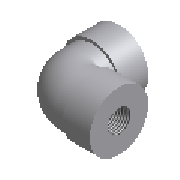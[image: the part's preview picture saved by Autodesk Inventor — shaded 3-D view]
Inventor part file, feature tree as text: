
AUTODESK INVENTOR PART (.ipt)
format: ipt  version: 2023.2 (Build 272271030, 271C)  size: 267,264 bytes
history: native  units: mm (DEFAULTED — no unit token found)
features: other x6, revolve x4, sketch x2
ambient origin geometry x8: Origin, YZ Plane, XZ Plane, XY Plane, X Axis, Y Axis, Z Axis, Center Point
bodies: Solid1 (feature_tree)
feature tree (12):
  sketch  "Sketch1"  dims[d0=18.320766mm d1=38.1mm d2=0.312398mm d3=0.312398mm]
  sketch  "Sketch2"  dims[d4=18.320766mm d5=38.1mm d6=13.55598mm d7=26.1112mm d8=13.55598mm d9=26.1112mm d10=0.0mm d11=9.9822mm d12=9.9822mm d13=17.145mm d14=0.0mm d101=90.0deg d102=90.0deg d105=25.4mm d106=0.0mm d107=25.4mm d108=0.0mm d15=33.274mm d16=16.637mm d17=33.274mm d18=16.637mm d19=34.29mm d20=34.29mm d21=9.9822mm d116=90.0deg d117=90.0deg d22=13.055641mm d23=0.0mm d122=0.0mm d123=0.0mm]
  revolve  "Revolve1"  [1 undecoded]
  revolve  "Revolve2"  [1 undecoded]
  revolve  "Revolve3"  [1 undecoded]
  revolve  "Revolve4"  [1 undecoded]
  other  "Work Axis1"
  other  "Work Point1"
  other  "Work Point2"
  other  "Work Axis2"
  other  "Work Point3"
  other  "Work Point4"
note: 4 required parameter values undecoded (feature->parameter linkage not recoverable at this tier; creation-order binding heuristic only, values carry confidence <= 0.55)
